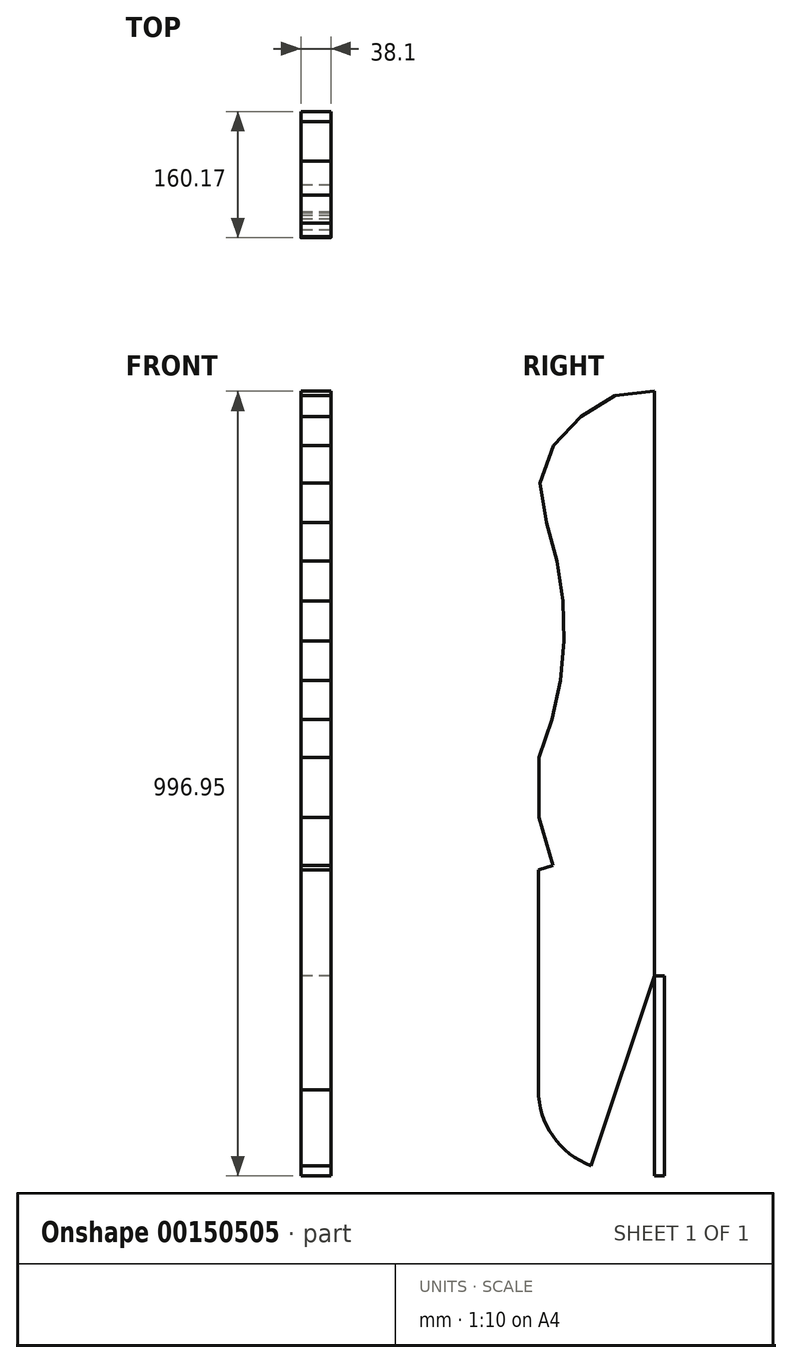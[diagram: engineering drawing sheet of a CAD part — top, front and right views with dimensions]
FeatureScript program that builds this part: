
annotation { "Feature Type Name" : "Feature", "Feature Type Description" : "" }
export const myFeature = defineFeature(function(context is Context, id is Id, definition is map)
    precondition{}
    {
        {
            var Q0;
            Q0=qCreatedBy(makeId("Right.planeOp"),FACE);
            var sketch = newSketch(context, id + "F0", { "sketchPlane" : qUnion([Q0])});
            skLineSegment(sketch, "E0", {"start": v(-143.71, 464.44) * mm, "end": v(-186.68, 437.35) * mm});
            skLineSegment(sketch, "E1", {"start": v(-186.68, 437.35) * mm, "end": v(-221.85, 400.7) * mm});
            skLineSegment(sketch, "E2", {"start": v(-221.85, 400.7) * mm, "end": v(-239, 352.87) * mm});
            skLineSegment(sketch, "E3", {"start": v(-239, 352.87) * mm, "end": v(-230.77, 302.74) * mm});
            skLineSegment(sketch, "E4", {"start": v(-143.71, 464.44) * mm, "end": v(-93.2, 469.82) * mm});
            skLineSegment(sketch, "E5", {"start": v(-93.2, 469.82) * mm, "end": v(-93.2, -273.13) * mm});
            skLineSegment(sketch, "E6", {"start": v(-240.66, -138.04) * mm, "end": v(-222.35, -132.78) * mm});
            skLineSegment(sketch, "E7", {"start": v(-222.35, -132.78) * mm, "end": v(-239.9, -71.75) * mm});
            skLineSegment(sketch, "E8", {"start": v(-239.9, -71.75) * mm, "end": v(-239.9, 4.45) * mm});
            skLineSegment(sketch, "E9", {"start": v(-240.66, -138.04) * mm, "end": v(-240.66, -417.44) * mm});
            skArc(sketch, "E10", {"start": v(-240.04, -407.27) * mm, "mid": v(-225.4, -472.1) * mm, "end": v(-173.8, -514) * mm});
            skArc(sketch, "E11", {"start": v(-239.9, 4.45) * mm, "mid": v(-208.18, 152.76) * mm, "end": v(-230.77, 302.74) * mm});
            skLineSegment(sketch, "E12", {"start": v(-173.8, -514) * mm, "end": v(-93.2, -273.13) * mm});
            skLineSegment(sketch, "E13", {"start": v(-230.77, 302.74) * mm, "end": v(-217.24, 253.77) * mm});
            skLineSegment(sketch, "E14", {"start": v(-217.24, 253.77) * mm, "end": v(-209.67, 203.54) * mm});
            skLineSegment(sketch, "E15", {"start": v(-209.67, 203.54) * mm, "end": v(-208.18, 152.76) * mm});
            skLineSegment(sketch, "E16", {"start": v(-208.18, 152.76) * mm, "end": v(-212.77, 102.17) * mm});
            skLineSegment(sketch, "E17", {"start": v(-212.77, 102.17) * mm, "end": v(-223.4, 52.5) * mm});
            skLineSegment(sketch, "E18", {"start": v(-223.4, 52.5) * mm, "end": v(-239.9, 4.45) * mm});
            skLineSegment(sketch, "E19", {"start": v(-93.2, -273.13) * mm, "end": v(-93.2, -527.13) * mm});
            skLineSegment(sketch, "E20.bottom", {"start": v(-93.2, -527.13) * mm, "end": v(-80.5, -527.13) * mm});
            skLineSegment(sketch, "E20.top", {"start": v(-93.2, -273.13) * mm, "end": v(-80.5, -273.13) * mm});
            skLineSegment(sketch, "E20.left", {"start": v(-93.2, -527.13) * mm, "end": v(-93.2, -273.13) * mm});
            skLineSegment(sketch, "E20.right", {"start": v(-80.5, -527.13) * mm, "end": v(-80.5, -273.13) * mm});
            skSolve(sketch);
        }
        {
            var Q0;
            Q0 = qSketchRegion(id + "F0", true);
            extrude(context, id + "F1", {"entities" : qUnion([Q0]), "depth" : 38.1 * mm});
        }
        {
            var Q0;
            Q0=makeQuery(id+"F0.imprint","IMPRINT",FACE,{"disambiguationData":[TD([[makeQuery(id+"F0.imprint","IMPRINT",EDGE,{"derivedFrom":sQuery(id+"F0.wireOp",EDGE,"E20.bottom")}),1.0]])]});
            extrude(context, id + "F2", {"entities" : qUnion([Q0]), "operationType" : NewBodyOperationType.ADD, "depth" : 25.4 * mm});
        }
    });
